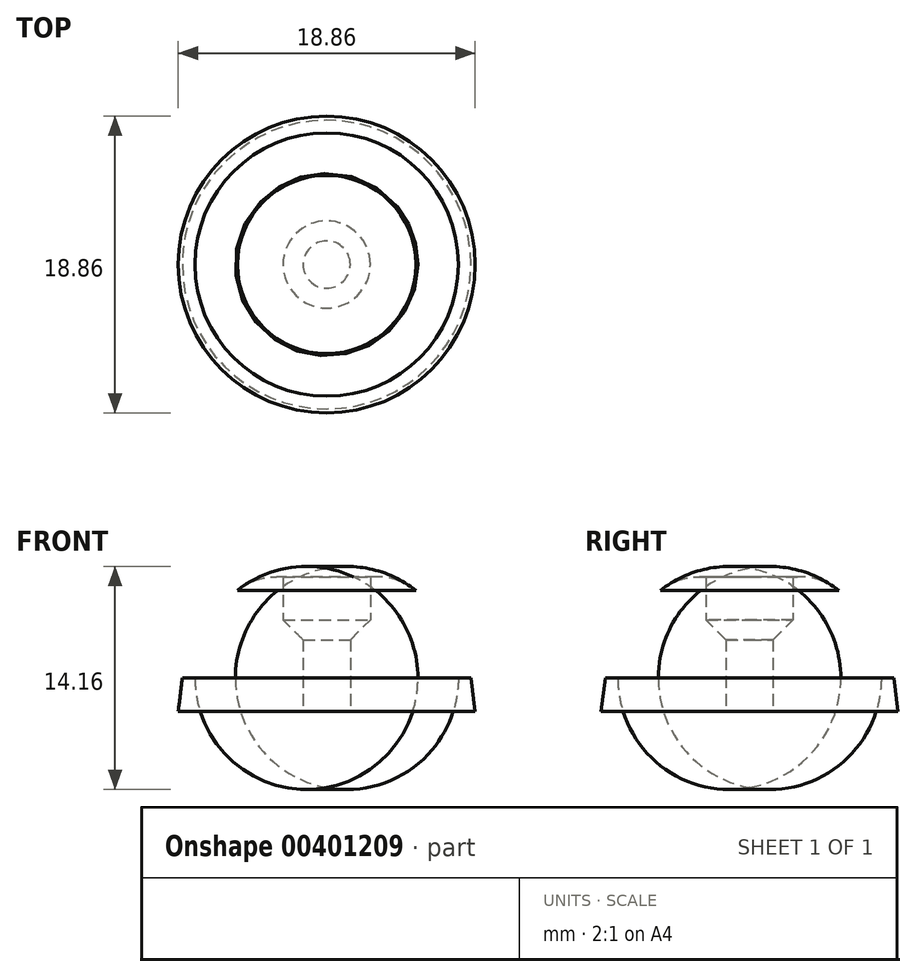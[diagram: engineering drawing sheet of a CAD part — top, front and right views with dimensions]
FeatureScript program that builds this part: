
annotation { "Feature Type Name" : "Feature", "Feature Type Description" : "" }
export const myFeature = defineFeature(function(context is Context, id is Id, definition is map)
    precondition{}
    {
        {
            var Q0;
            Q0=qCreatedBy(makeId("Front.planeOp"),FACE);
            var sketch = newSketch(context, id + "F0", { "sketchPlane" : qUnion([Q0])});
            skLineSegment(sketch, "E0", {"start": v(-1.5, 0) * mm, "end": v(-9.43, 0) * mm});
            skLineSegment(sketch, "E1", {"start": v(-9.43, 0) * mm, "end": v(-9.16, 2.12) * mm});
            skLineSegment(sketch, "E2", {"start": v(-9.16, 2.12) * mm, "end": v(-8.36, 2.12) * mm});
            skArc(sketch, "E3", {"start": v(-8.36, 2.12) * mm, "mid": v(-7.25, 5.93) * mm, "end": v(-4.27, 8.54) * mm});
            skLineSegment(sketch, "E4", {"start": v(-2.77, 8.54) * mm, "end": v(-2.77, 5.8) * mm});
            skLineSegment(sketch, "E5", {"start": v(-2.77, 5.8) * mm, "end": v(-1.5, 4.54) * mm});
            skLineSegment(sketch, "E6", {"start": v(-1.5, 4.54) * mm, "end": v(-1.5, 0) * mm});
            skLineSegment(sketch, "E7", {"start": v(0, 0) * mm, "end": v(0, 8.1) * mm, "construction": true});
            skLineSegment(sketch, "E8", {"start": v(-4.27, 8.54) * mm, "end": v(-2.77, 8.54) * mm});
            skSolve(sketch);
        }
        {
            var Q0;
            Q0=makeQuery(id+"F0.imprint","IMPRINT",FACE,{"disambiguationData":[TD([[makeQuery(id+"F0.imprint","IMPRINT",EDGE,{"derivedFrom":sQuery(id+"F0.wireOp",EDGE,"E0")}),-1.0]])]});
            var Q1;
            Q1=sQuery(id+"F0.wireOp",EDGE,"E7");
            revolve(context, id + "F1", {"entities" : qUnion([Q0]), "axis" : qUnion([Q1]), "revolveType" : RevolveType.FULL});
        }
        {
            var Q0;
            Q0=makeQuery(id+"F1.opRevolve","SWEPT_EDGE",EDGE,{"disambiguationData":[OSD([sQuery(id+"F0.wireOp",EDGE,"E3"),sQuery(id+"F0.wireOp",EDGE,"E8")])]});
            fillet(context, id + "F2", {"entities" : qUnion([Q0]), "radius" : 4 * mm, "tangentPropagation" : true, "allowEdgeOverflow" : false});
        }
    });
